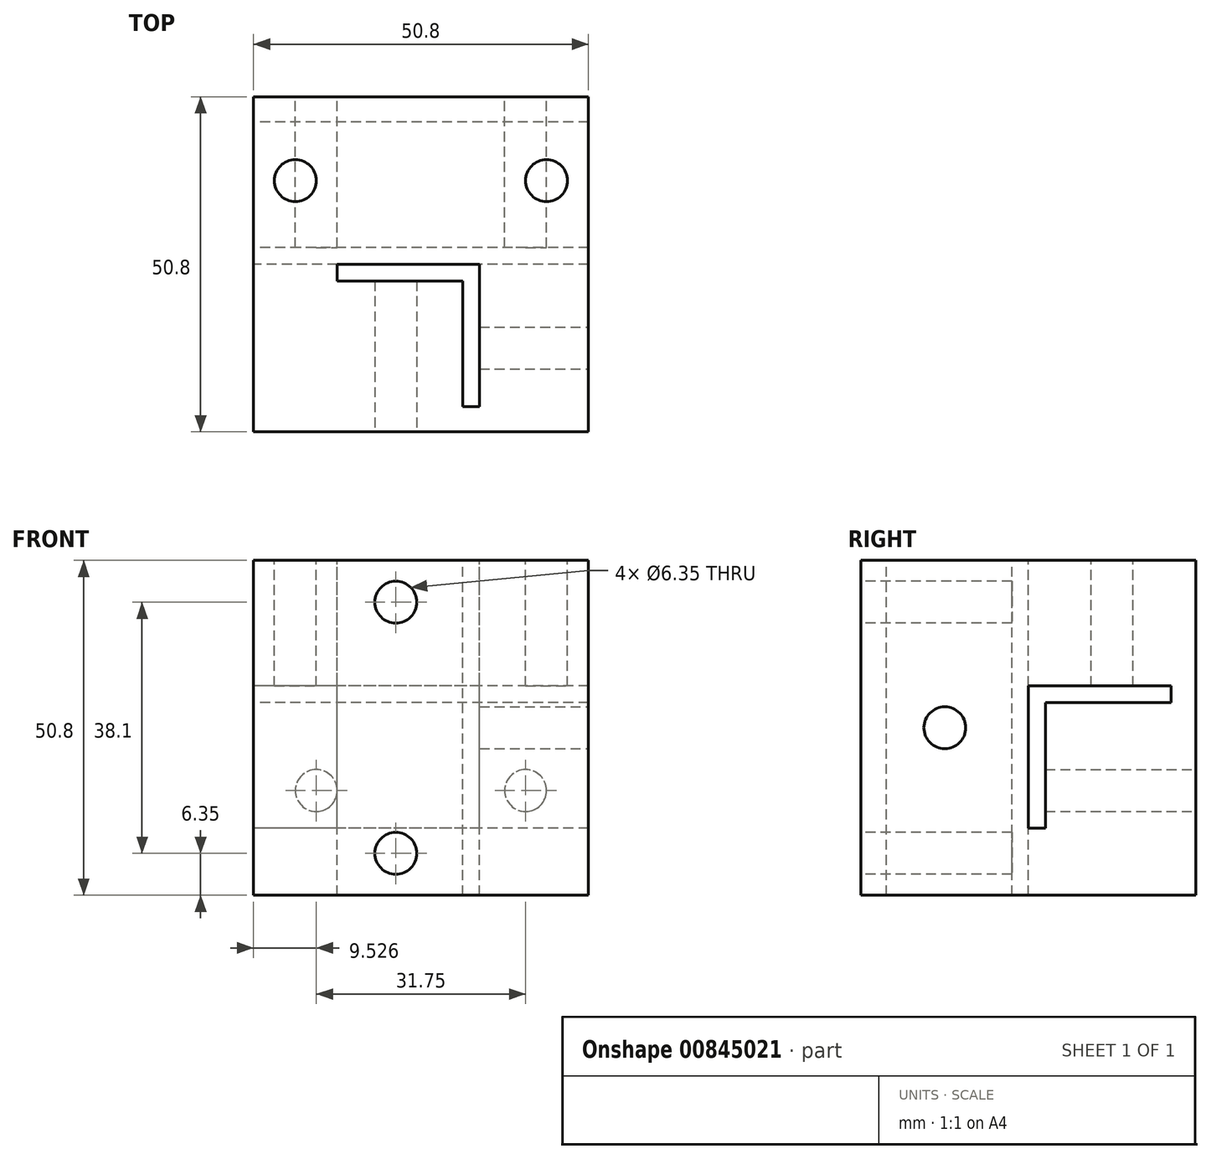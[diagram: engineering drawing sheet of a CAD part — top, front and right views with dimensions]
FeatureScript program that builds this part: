
annotation { "Feature Type Name" : "Feature", "Feature Type Description" : "" }
export const myFeature = defineFeature(function(context is Context, id is Id, definition is map)
    precondition{}
    {
        {
            var Q0;
            Q0=qCreatedBy(makeId("Top.planeOp"),FACE);
            var sketch = newSketch(context, id + "F0", { "sketchPlane" : qUnion([Q0])});
            skLineSegment(sketch, "E0.bottom", {"start": v(-16.15, -10.49) * mm, "end": v(34.65, -10.49) * mm});
            skLineSegment(sketch, "E0.top", {"start": v(-16.15, 40.31) * mm, "end": v(34.65, 40.31) * mm});
            skLineSegment(sketch, "E0.left", {"start": v(-16.15, -10.49) * mm, "end": v(-16.15, 40.31) * mm});
            skLineSegment(sketch, "E0.right", {"start": v(34.65, -10.49) * mm, "end": v(34.65, 40.31) * mm});
            skSolve(sketch);
        }
        {
            var Q0;
            Q0 = qSketchRegion(id + "F0", true);
            extrude(context, id + "F1", {"entities" : qUnion([Q0]), "depth" : 50.8 * mm, "offsetDistance" : 25.4 * mm});
        }
        {
            var Q0;
            Q0=makeQuery(id+"F1.opExtrude","CAP_FACE",FACE,{"disambiguationData":[OSD([sQuery(id+"F0.wireOp",EDGE,"E0.bottom"),sQuery(id+"F0.wireOp",EDGE,"E0.top"),sQuery(id+"F0.wireOp",EDGE,"E0.left"),sQuery(id+"F0.wireOp",EDGE,"E0.right")])],"isStart":false});
            var sketch = newSketch(context, id + "F2", { "sketchPlane" : qUnion([Q0])});
            skLineSegment(sketch, "E1", {"start": v(-3.45, 12.37) * mm, "end": v(15.6, 12.37) * mm});
            skLineSegment(sketch, "E2", {"start": v(15.6, 12.37) * mm, "end": v(15.6, -6.68) * mm});
            skLineSegment(sketch, "E3", {"start": v(15.6, -6.68) * mm, "end": v(18.14, -6.68) * mm});
            skLineSegment(sketch, "E4", {"start": v(18.14, -6.68) * mm, "end": v(18.14, 14.91) * mm});
            skLineSegment(sketch, "E5", {"start": v(18.14, 14.91) * mm, "end": v(-3.45, 14.91) * mm});
            skLineSegment(sketch, "E6", {"start": v(-3.45, 14.91) * mm, "end": v(-3.45, 12.37) * mm});
            skSolve(sketch);
        }
        {
            var Q0;
            Q0 = qSketchRegion(id + "F2", true);
            extrude(context, id + "F3", {"entities" : qUnion([Q0]), "operationType" : NewBodyOperationType.REMOVE, "endBound" : BoundingType.UP_TO_NEXT, "oppositeDirection" : true, "depth" : 25.4 * mm, "offsetDistance" : 25.4 * mm});
        }
        {
            var Q0;
            Q0=makeQuery(id+"F1.opExtrude","SWEPT_FACE",FACE,{"disambiguationData":[OSD([sQuery(id+"F0.wireOp",EDGE,"E0.left")])]});
            var sketch = newSketch(context, id + "F4", { "sketchPlane" : qUnion([Q0])});
            skLineSegment(sketch, "E7", {"start": v(-14.91, 31.75) * mm, "end": v(-14.91, 10.16) * mm});
            skLineSegment(sketch, "E8", {"start": v(-14.91, 10.16) * mm, "end": v(-17.45, 10.16) * mm});
            skLineSegment(sketch, "E9", {"start": v(-17.45, 10.16) * mm, "end": v(-17.45, 29.21) * mm});
            skLineSegment(sketch, "E10", {"start": v(-17.45, 29.21) * mm, "end": v(-36.5, 29.21) * mm});
            skLineSegment(sketch, "E11", {"start": v(-36.5, 29.21) * mm, "end": v(-36.5, 31.75) * mm});
            skLineSegment(sketch, "E12", {"start": v(-36.5, 31.75) * mm, "end": v(-14.91, 31.75) * mm});
            skSolve(sketch);
        }
        {
            var Q0;
            Q0 = qSketchRegion(id + "F4", true);
            var Q1;
            Q1=makeQuery(id+"F1.opExtrude","SWEPT_FACE",FACE,{"disambiguationData":[OSD([sQuery(id+"F0.wireOp",EDGE,"E0.right")])]});
            extrude(context, id + "F5", {"entities" : qUnion([Q0]), "operationType" : NewBodyOperationType.REMOVE, "endBound" : BoundingType.UP_TO_SURFACE, "oppositeDirection" : true, "depth" : 25.4 * mm, "endBoundEntityFace" : qUnion([Q1]), "offsetDistance" : 25.4 * mm});
        }
        {
            var Q0;
            Q0=makeQuery(id+"F1.opExtrude","SWEPT_FACE",FACE,{"disambiguationData":[OSD([sQuery(id+"F0.wireOp",EDGE,"E0.bottom")])]});
            var sketch = newSketch(context, id + "F6", { "sketchPlane" : qUnion([Q0])});
            skCircle(sketch, "E13", {"center": v(5.44, 44.45) * mm, "radius": 3.18 * mm});
            skCircle(sketch, "E14", {"center": v(5.44, 6.35) * mm, "radius": 3.17 * mm});
            skSolve(sketch);
        }
        {
            var Q0;
            Q0 = qSketchRegion(id + "F6", true);
            extrude(context, id + "F7", {"entities" : qUnion([Q0]), "operationType" : NewBodyOperationType.REMOVE, "endBound" : BoundingType.UP_TO_NEXT, "oppositeDirection" : true, "depth" : 25.4 * mm, "offsetDistance" : 25.4 * mm});
        }
        {
            var Q0;
            Q0=makeQuery(id+"F1.opExtrude","SWEPT_FACE",FACE,{"disambiguationData":[OSD([sQuery(id+"F0.wireOp",EDGE,"E0.right")])]});
            var sketch = newSketch(context, id + "F8", { "sketchPlane" : qUnion([Q0])});
            skCircle(sketch, "E15", {"center": v(2.21, 25.4) * mm, "radius": 3.17 * mm});
            skSolve(sketch);
        }
        {
            var Q0;
            Q0 = qSketchRegion(id + "F8", true);
            extrude(context, id + "F9", {"entities" : qUnion([Q0]), "operationType" : NewBodyOperationType.REMOVE, "endBound" : BoundingType.UP_TO_NEXT, "oppositeDirection" : true, "depth" : 25.4 * mm, "offsetDistance" : 25.4 * mm});
        }
        {
            var Q0;
            Q0=makeQuery(id+"F1.opExtrude","CAP_FACE",FACE,{"disambiguationData":[OSD([sQuery(id+"F0.wireOp",EDGE,"E0.bottom"),sQuery(id+"F0.wireOp",EDGE,"E0.top"),sQuery(id+"F0.wireOp",EDGE,"E0.left"),sQuery(id+"F0.wireOp",EDGE,"E0.right")])],"isStart":false});
            var sketch = newSketch(context, id + "F10", { "sketchPlane" : qUnion([Q0])});
            skCircle(sketch, "E16", {"center": v(28.3, 27.61) * mm, "radius": 3.18 * mm});
            skCircle(sketch, "E17", {"center": v(-9.8, 27.61) * mm, "radius": 3.18 * mm});
            skSolve(sketch);
        }
        {
            var Q0;
            Q0 = qSketchRegion(id + "F10", true);
            extrude(context, id + "F11", {"entities" : qUnion([Q0]), "operationType" : NewBodyOperationType.REMOVE, "endBound" : BoundingType.UP_TO_NEXT, "oppositeDirection" : true, "depth" : 25.4 * mm, "offsetDistance" : 25.4 * mm});
        }
        {
            var Q0;
            Q0=makeQuery(id+"F1.opExtrude","SWEPT_FACE",FACE,{"disambiguationData":[OSD([sQuery(id+"F0.wireOp",EDGE,"E0.top")])]});
            var sketch = newSketch(context, id + "F12", { "sketchPlane" : qUnion([Q0])});
            skCircle(sketch, "E18", {"center": v(-25.13, 15.88) * mm, "radius": 3.18 * mm});
            skCircle(sketch, "E19", {"center": v(6.62, 15.88) * mm, "radius": 3.18 * mm});
            skSolve(sketch);
        }
        {
            var Q0;
            Q0 = qSketchRegion(id + "F12", true);
            extrude(context, id + "F13", {"entities" : qUnion([Q0]), "operationType" : NewBodyOperationType.REMOVE, "endBound" : BoundingType.UP_TO_NEXT, "oppositeDirection" : true, "depth" : 25.4 * mm, "offsetDistance" : 25.4 * mm});
        }
    });
